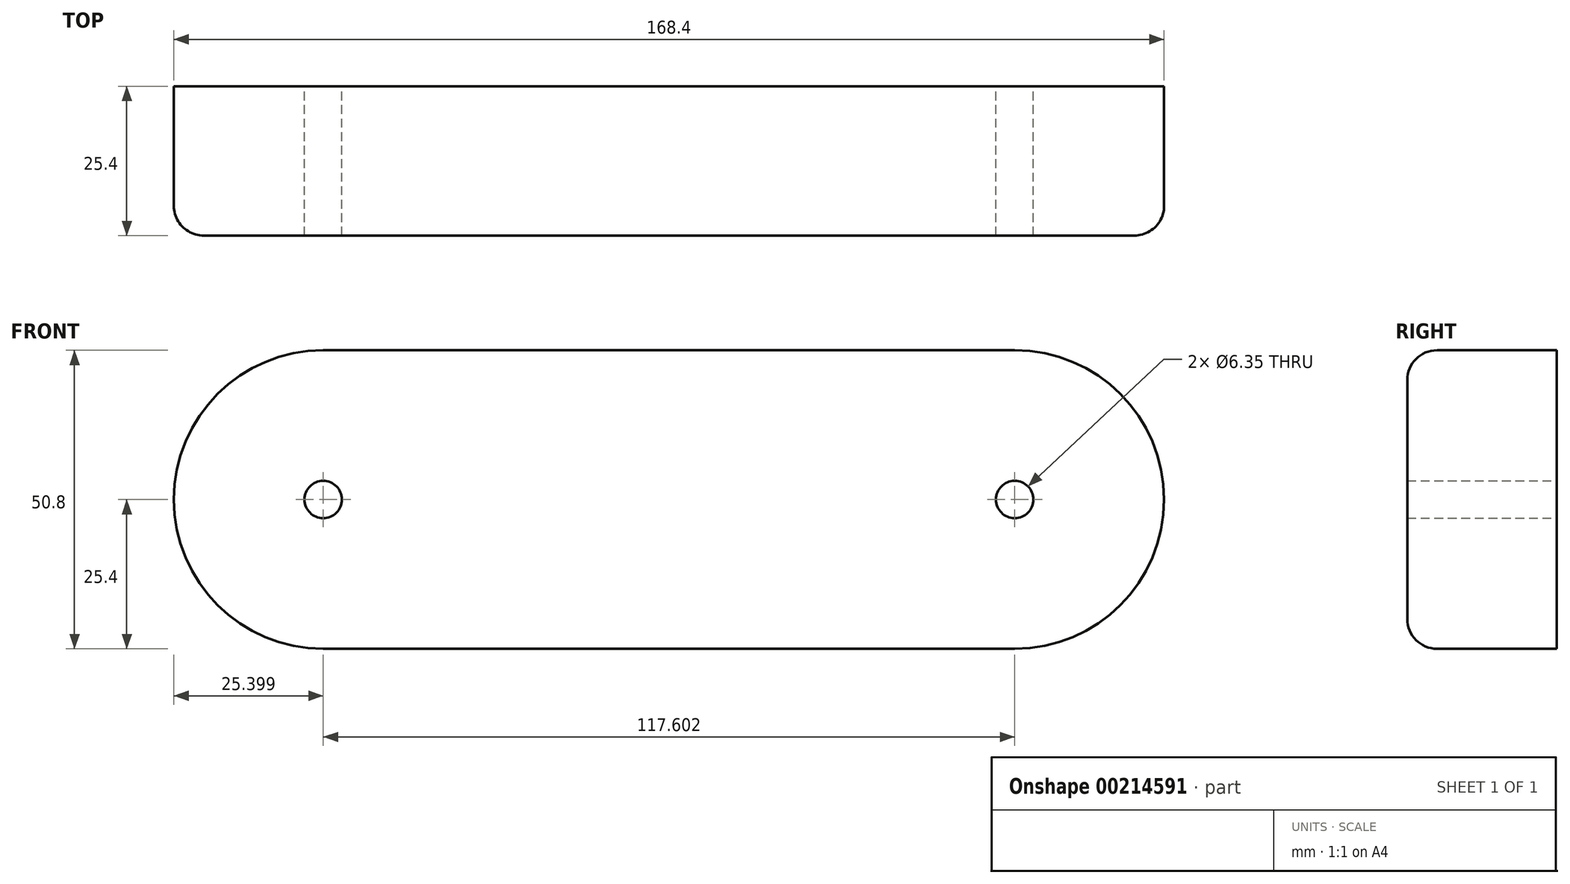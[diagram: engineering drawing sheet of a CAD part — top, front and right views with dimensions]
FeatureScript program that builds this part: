
annotation { "Feature Type Name" : "Feature", "Feature Type Description" : "" }
export const myFeature = defineFeature(function(context is Context, id is Id, definition is map)
    precondition{}
    {
        {
            var Q0;
            Q0=qCreatedBy(makeId("Front.planeOp"),FACE);
            var sketch = newSketch(context, id + "F0", { "sketchPlane" : qUnion([Q0])});
            skLineSegment(sketch, "E0", {"start": v(0, 0) * mm, "end": v(-58.8, 0) * mm});
            skLineSegment(sketch, "E1", {"start": v(0, 0) * mm, "end": v(58.8, 0) * mm});
            skCircle(sketch, "E2", {"center": v(-58.8, 0) * mm, "radius": 3.18 * mm});
            skCircle(sketch, "E3", {"center": v(58.8, 0) * mm, "radius": 3.17 * mm});
            skLineSegment(sketch, "E4", {"start": v(-58.8, 0) * mm, "end": v(-58.8, 37.44) * mm});
            skLineSegment(sketch, "E5", {"start": v(-58.8, 37.44) * mm, "end": v(-58.8, 0) * mm});
            skLineSegment(sketch, "E6", {"start": v(-58.8, -31.46) * mm, "end": v(-58.8, 3.17) * mm});
            skLineSegment(sketch, "E7", {"start": v(58.8, 0) * mm, "end": v(58.8, 46.4) * mm});
            skLineSegment(sketch, "E8", {"start": v(58.8, 46.4) * mm, "end": v(58.8, 0) * mm});
            skLineSegment(sketch, "E9", {"start": v(58.8, -36.7) * mm, "end": v(58.8, 0) * mm});
            skLineSegment(sketch, "E10", {"start": v(-58.8, 25.4) * mm, "end": v(58.8, 25.4) * mm});
            skLineSegment(sketch, "E11", {"start": v(-58.8, -25.4) * mm, "end": v(58.8, -25.4) * mm});
            skArc(sketch, "E12", {"start": v(-58.8, 25.4) * mm, "mid": v(-84.2, 0) * mm, "end": v(-58.8, -25.4) * mm});
            skArc(sketch, "E13", {"start": v(58.8, -25.4) * mm, "mid": v(84.2, 0) * mm, "end": v(58.8, 25.4) * mm});
            skSolve(sketch);
        }
        {
            var Q0;
            {var subQ5=sQuery(id+"F0.wireOp",EDGE,"E13");Q0=makeQuery(id+"F0.imprint","IMPRINT",FACE,{"disambiguationData":[TD([[makeQuery(id+"F0.imprint","IMPRINT",EDGE,{"derivedFrom":subQ5}),1.0]])]});}
            var Q1;
            {var subQ5=sQuery(id+"F0.wireOp",EDGE,"E10");Q1=makeQuery(id+"F0.imprint","IMPRINT",FACE,{"disambiguationData":[TD([[makeQuery(id+"F0.imprint","IMPRINT",EDGE,{"derivedFrom":subQ5}),-1.0]])]});}
            var Q2;
            {var subQ11=sQuery(id+"F0.wireOp",EDGE,"E11");Q2=makeQuery(id+"F0.imprint","IMPRINT",FACE,{"disambiguationData":[TD([[makeQuery(id+"F0.imprint","IMPRINT",EDGE,{"derivedFrom":subQ11}),1.0]])]});}
            var Q3;
            {var subQ5=sQuery(id+"F0.wireOp",EDGE,"E12");Q3=makeQuery(id+"F0.imprint","IMPRINT",FACE,{"disambiguationData":[TD([[makeQuery(id+"F0.imprint","IMPRINT",EDGE,{"derivedFrom":subQ5}),1.0]])]});}
            extrude(context, id + "F1", {"entities" : qUnion([Q0, Q1, Q2, Q3]), "endBound" : BoundingType.SYMMETRIC, "depth" : 25.4 * mm});
        }
        {
            var Q0;
            Q0=makeQuery(id+"F1.opExtrude","CAP_EDGE",EDGE,{"disambiguationData":[OSD([sQuery(id+"F0.wireOp",EDGE,"E12")])],"isStart":false});
            var Q1;
            Q1=makeQuery(id+"F1.opExtrude","CAP_EDGE",EDGE,{"disambiguationData":[OSD([sQuery(id+"F0.wireOp",EDGE,"E10")])],"isStart":false});
            fillet(context, id + "F2", {"entities" : qUnion([Q0, Q1]), "radius" : 5.08 * mm, "tangentPropagation" : true, "allowEdgeOverflow" : false});
        }
    });
